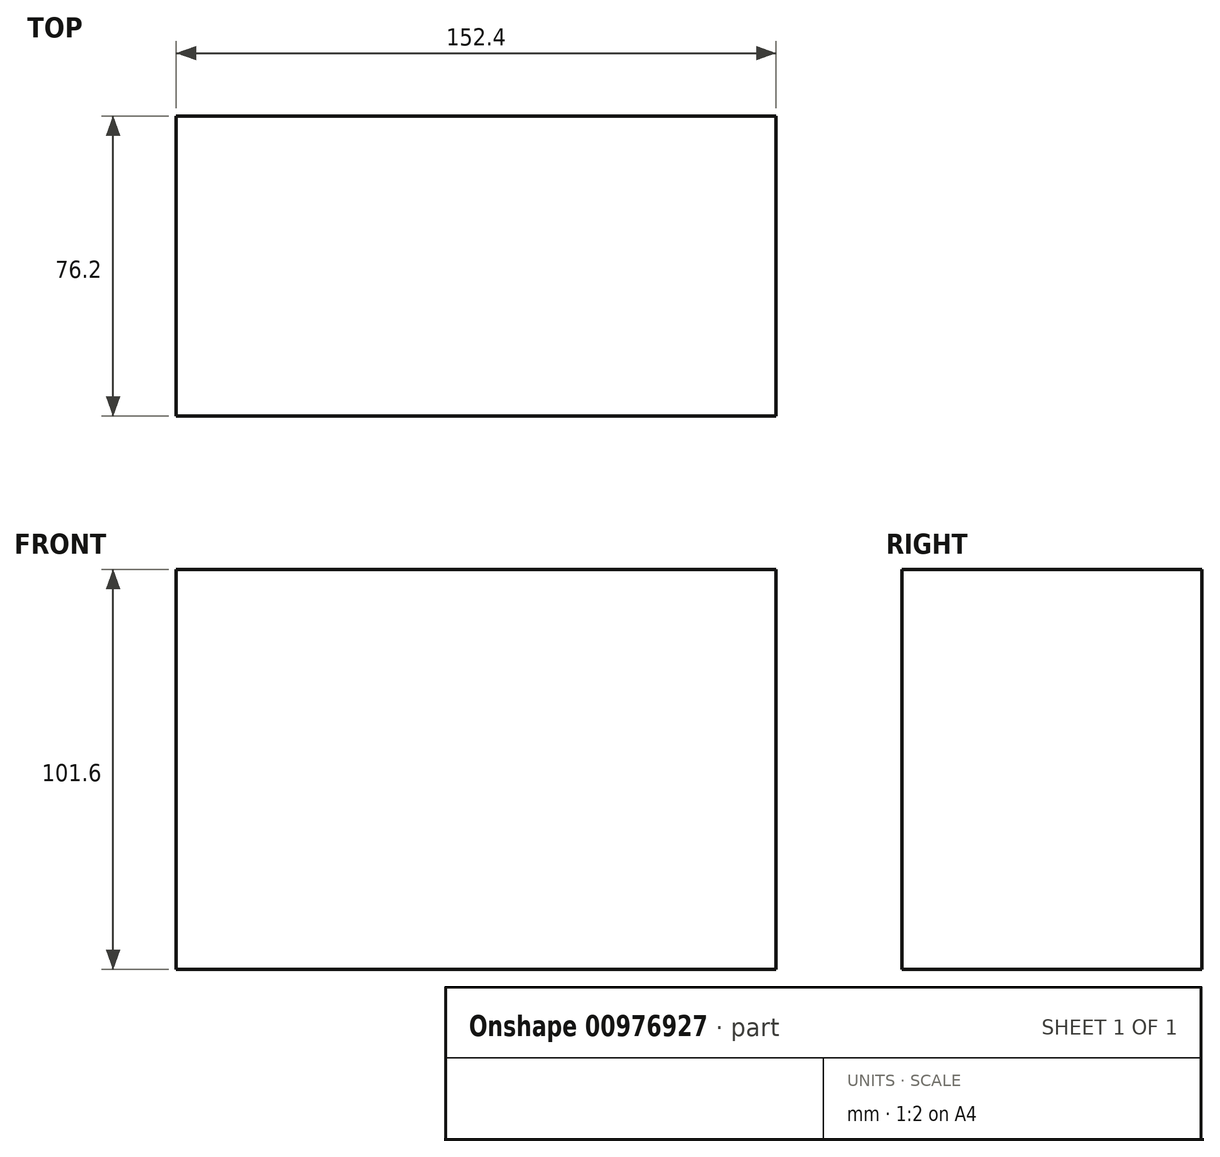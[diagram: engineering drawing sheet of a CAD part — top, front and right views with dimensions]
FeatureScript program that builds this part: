
annotation { "Feature Type Name" : "Feature", "Feature Type Description" : "" }
export const myFeature = defineFeature(function(context is Context, id is Id, definition is map)
    precondition{}
    {
        {
            var Q0;
            Q0=qCreatedBy(makeId("Front.planeOp"),FACE);
            var sketch = newSketch(context, id + "F0", { "sketchPlane" : qUnion([Q0])});
            skLineSegment(sketch, "E0.bottom", {"start": v(45.24, 9.87) * mm, "end": v(-107.16, 9.87) * mm});
            skLineSegment(sketch, "E0.top", {"start": v(45.24, 111.47) * mm, "end": v(-107.16, 111.47) * mm});
            skLineSegment(sketch, "E0.left", {"start": v(45.24, 9.87) * mm, "end": v(45.24, 111.47) * mm});
            skLineSegment(sketch, "E0.right", {"start": v(-107.16, 9.87) * mm, "end": v(-107.16, 111.47) * mm});
            skPoint(sketch, "E0.middle", {"position": v(-30.96, 60.67) * mm});
            skSolve(sketch);
        }
        {
            var Q0;
            Q0=makeQuery(id+"F0.imprint","IMPRINT",FACE,{"disambiguationData":[TD([[makeQuery(id+"F0.imprint","IMPRINT",EDGE,{"derivedFrom":sQuery(id+"F0.wireOp",EDGE,"E0.bottom")}),-1.0]])]});
            extrude(context, id + "F1", {"entities" : qUnion([Q0]), "depth" : 76.2 * mm, "offsetDistance" : 25.4 * mm});
        }
    });
